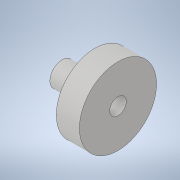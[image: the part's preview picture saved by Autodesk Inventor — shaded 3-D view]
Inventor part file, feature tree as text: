
AUTODESK INVENTOR PART (.ipt)
format: ipt  version: 2021 (Build 250183000, 183)  size: 106,496 bytes
history: native  units: in
note: dims shown in document units (in); Inventor stores cm internally (conversion verified against a paired STEP export)
features: extrude x2, sketch x2
ambient origin geometry x8: Origin, YZ Plane, XZ Plane, XY Plane, X Axis, Y Axis, Z Axis, Center Point
bodies: Solid1 (feature_tree)
feature tree (4):
  extrude  "Extrusion1"  Depth=0.268in
  extrude  "Extrusion2"  Depth=0.375in
  sketch  "Sketch1"  dims[d0=0.394in d1=0.268in]
  sketch  "Sketch2"  dims[d2=0.532in d3=0.0in d4=1.25in d5=0.375in d6=0.0in d7=0.268in]
